# Revit family: IRIS-PS-BB 4500-8xx-xx-O
name_source: partatom
category: Leuchten
revit_build: Autodesk Revit 2017 (Build: 20190508_0315(x64)
units: mm (PartAtom-declared; Revit-internal decimal feet)

## family parameters
Basisbauteil = Fläche
Beim Laden mit Abzugskörper schneiden = Nein
Bemaßung runder Anschluss = Durchmesser verwenden
Gemeinsam genutzt = Nein
Lichtquelle = Ja
OmniClass-Nummer = 23.80.70.11
OmniClass-Titel = Luminaries for Internal Lighting
Raumberechnungspunkt = Nein
Teiletyp = Normal

## types (5) — shared parameters
Baugruppenkennzeichen = D5020200
Datei für fotometrisches Netz = IRIS-PS 4500-840-ND-O.IES
Emissionsform beim Rendern sichtbar = Nein
Farbfilter = 16777215
Farbtemperaturverschiebung bei Dämpfen der Lampe = <Keine Auswahl>
Hersteller = RIDI Leuchten GmbH
Lampe = LED
Neigungswinkel = 90.00°
Scheinlast = 33 VA
URL = www.spectral-lighting.com
Von Kreisdurchmesser aussenden = 375 mm  [stored 1.23031 ft]
brand = Spectral
conformity mark = CE
electrical safety class = 1
height = 50 mm  [stored 0.164042 ft]
ingress protection (IP) code = IP20
length = 375 mm  [stored 1.23031 ft]
nominal frequency = 50-60Hz
nominal voltage = 230
rated input power = 33
voltage type (AC, DC, UC) = AC
weight = 2.0 kg
width = 375 mm  [stored 1.23031 ft]
zero-valued in all types: Vorgabe-Ansicht

## per-type parameters (varying)
| type | Modell |
| IRIS-PS-BB 4500-830-ND-O | SPI0000238 |
| IRIS-PS-BB 4500-840-ND-O | SPI0000239 |
| IRIS-PS-BB 4500-830-DA-O | SPI0000240 |
| IRIS-PS-BB 4500-840-DA-O | SPI0000241 |
| IRIS-PS-BB 4500-8TW-DA-O | SPI0000242 |

note: column(s) folded — value = type name in every type: product name

note: [stored X ft] marks values corroborated as IEEE doubles in the binary element streams (Revit-internal decimal feet)
